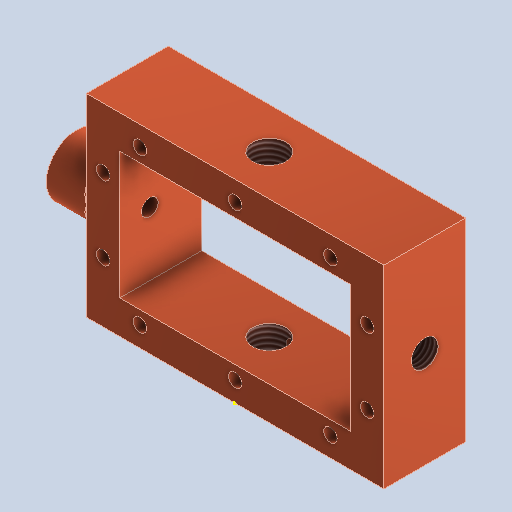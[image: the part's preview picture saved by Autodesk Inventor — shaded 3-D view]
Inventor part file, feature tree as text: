
AUTODESK INVENTOR PART (.ipt)
format: ipt  version: 2025.1 (Build 291241000, 241)  size: 222,720 bytes
history: native  units: mm
features: sketch x9, other x3, plane x2
ambient origin geometry x8: Origin, YZ Plane, XZ Plane, XY Plane, X Axis, Y Axis, Z Axis, Center Point
bodies: Volumenkörper1 (feature_tree)
feature tree (14):
  other  "1152_body.ipt"
  other  "Volumenkörper1::1152_body.ipt"
  other  "TaggingFeature1"
  sketch  "Skizze1"  dims[d0=10.0mm]
  sketch  "Skizze2"
  sketch  "Skizze3"
  sketch  "Skizze4"
  sketch  "Skizze5"
  sketch  "Skizze6"
  sketch  "Skizze7"
  sketch  "Skizze9"
  sketch  "Skizze10"
  plane  "Arbeitsebene1"
  plane  "Arbeitsebene3"
